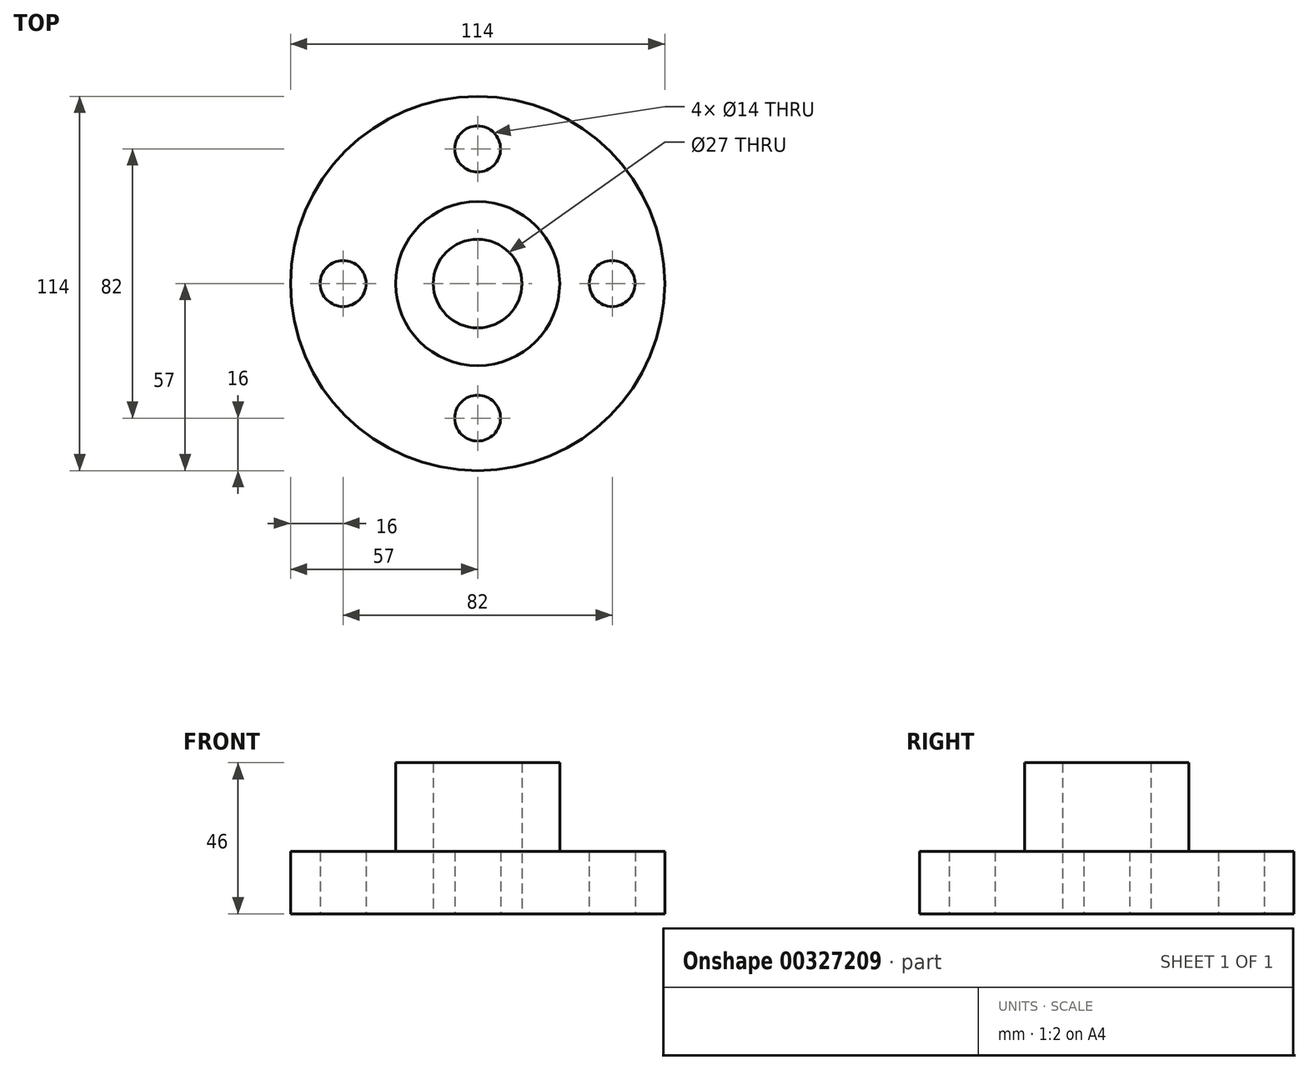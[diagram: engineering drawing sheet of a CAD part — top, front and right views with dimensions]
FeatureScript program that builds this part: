
annotation { "Feature Type Name" : "Feature", "Feature Type Description" : "" }
export const myFeature = defineFeature(function(context is Context, id is Id, definition is map)
    precondition{}
    {
        {
            var Q0;
            Q0=qCreatedBy(makeId("Top.planeOp"),FACE);
            var sketch = newSketch(context, id + "F0", { "sketchPlane" : qUnion([Q0])});
            skCircle(sketch, "E0", {"center": v(0, 0) * mm, "radius": 57 * mm});
            skCircle(sketch, "E1", {"center": v(0, 0) * mm, "radius": 13.5 * mm});
            skCircle(sketch, "E2", {"center": v(0, 41) * mm, "radius": 7 * mm});
            skCircle(sketch, "E3.1.0", {"center": v(-41, 0) * mm, "radius": 7 * mm});
            skCircle(sketch, "E3.2.0", {"center": v(0, -41) * mm, "radius": 7 * mm});
            skCircle(sketch, "E3.3.0", {"center": v(41, 0) * mm, "radius": 7 * mm});
            skSolve(sketch);
        }
        {
            var Q0;
            Q0 = qSketchRegion(id + "F0", true);
            extrude(context, id + "F1", {"entities" : qUnion([Q0]), "depth" : 19 * mm});
        }
        {
            var Q0;
            Q0=makeQuery(id+"F1.opExtrude","CAP_FACE",FACE,{"disambiguationData":[OSD([sQuery(id+"F0.wireOp",EDGE,"E0"),sQuery(id+"F0.wireOp",EDGE,"E1"),sQuery(id+"F0.wireOp",EDGE,"E2"),sQuery(id+"F0.wireOp",EDGE,"E3.1.0"),sQuery(id+"F0.wireOp",EDGE,"E3.2.0"),sQuery(id+"F0.wireOp",EDGE,"E3.3.0")])],"isStart":false});
            var sketch = newSketch(context, id + "F2", { "sketchPlane" : qUnion([Q0])});
            skCircle(sketch, "E4", {"center": v(0, 0) * mm, "radius": 25 * mm});
            skCircle(sketch, "E5", {"center": v(0, 0) * mm, "radius": 13.5 * mm});
            skSolve(sketch);
        }
        {
            var Q0;
            Q0 = qSketchRegion(id + "F2", true);
            extrude(context, id + "F3", {"entities" : qUnion([Q0]), "operationType" : NewBodyOperationType.ADD, "depth" : (46 - 19) * mm});
        }
    });
